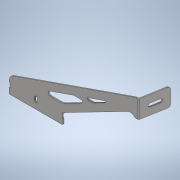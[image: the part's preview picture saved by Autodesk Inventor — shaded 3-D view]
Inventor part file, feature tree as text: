
AUTODESK INVENTOR PART (.ipt)
format: ipt  version: 2020 (Build 240168000, 168)  size: 418,304 bytes
history: native  units: mm
features: other x3, extrude x1, plane x1
ambient origin geometry x8: Origin, YZ Plane, XZ Plane, XY Plane, X Axis, Y Axis, Z Axis, Center Point
bodies: Body1 (feature_tree)
feature tree (5):
  other  "實體1"
  extrude  "擠出1"  Depth=130.0mm
  other  "折彎零件1"
  plane  "工作平面1"
  other  "定義1"
